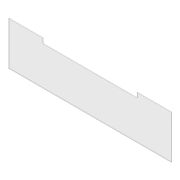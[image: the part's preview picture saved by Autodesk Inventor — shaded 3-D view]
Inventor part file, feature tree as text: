
AUTODESK INVENTOR PART (.ipt)
format: ipt  version: unknown  size: 180,224 bytes
history: native  units: in
note: dims shown in document units (in); Inventor stores cm internally (conversion verified against a paired STEP export)
features: extrude x2, sketch x2
ambient origin geometry x8: Origin, YZ Plane, XZ Plane, XY Plane, X Axis, Y Axis, Z Axis, Center Point
bodies: Solid1 (feature_tree)
feature tree (4):
  extrude  "Extrusion1"  Depth=17.875in
  extrude  "Extrusion2"  Depth=14.0in
  sketch  "Sketch1"  dims[d0=67.0in d1=17.875in]
  sketch  "Sketch4"  dims[d2=0.25in d3=0.0in d44=14.0in d45=14.0in d46=2.0in d47=0.5in d48=1.0in d49=0.0in]
